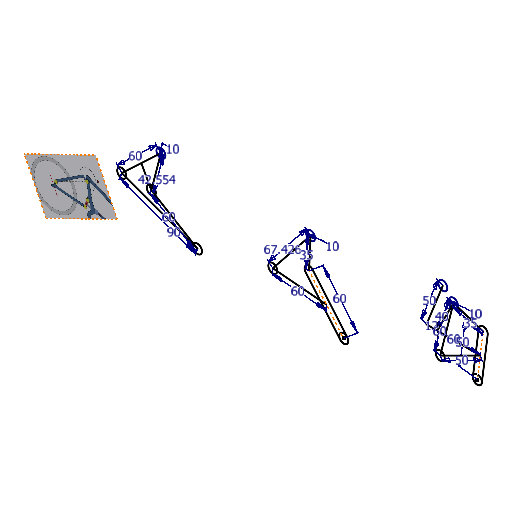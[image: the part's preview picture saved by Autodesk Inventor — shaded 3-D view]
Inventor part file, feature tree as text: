
AUTODESK INVENTOR PART (.ipt)
format: ipt  version: 2025 (Build 290162000, 162)  size: 162,816 bytes
history: native  units: mm
features: sketch x1, other x1
ambient origin geometry x8: Origin, YZ Plane, XZ Plane, XY Plane, X Axis, Y Axis, Z Axis, Center Point
feature tree (2):
  sketch  "Sketch1"  dims[d47=10.0mm d50=60.0mm d52=60.0mm d53=90.0mm d64=42.554077mm d95=10.0mm d98=60.0mm d148=60.0mm d149=35.0mm d160=67.42577mm d199=10.0mm d200=50.0mm d201=50.0mm d202=35.0mm d203=60.0mm d214=50.0mm d215=60.0mm d240=12.0mm d241=40.0mm]
  other  "Image1"
